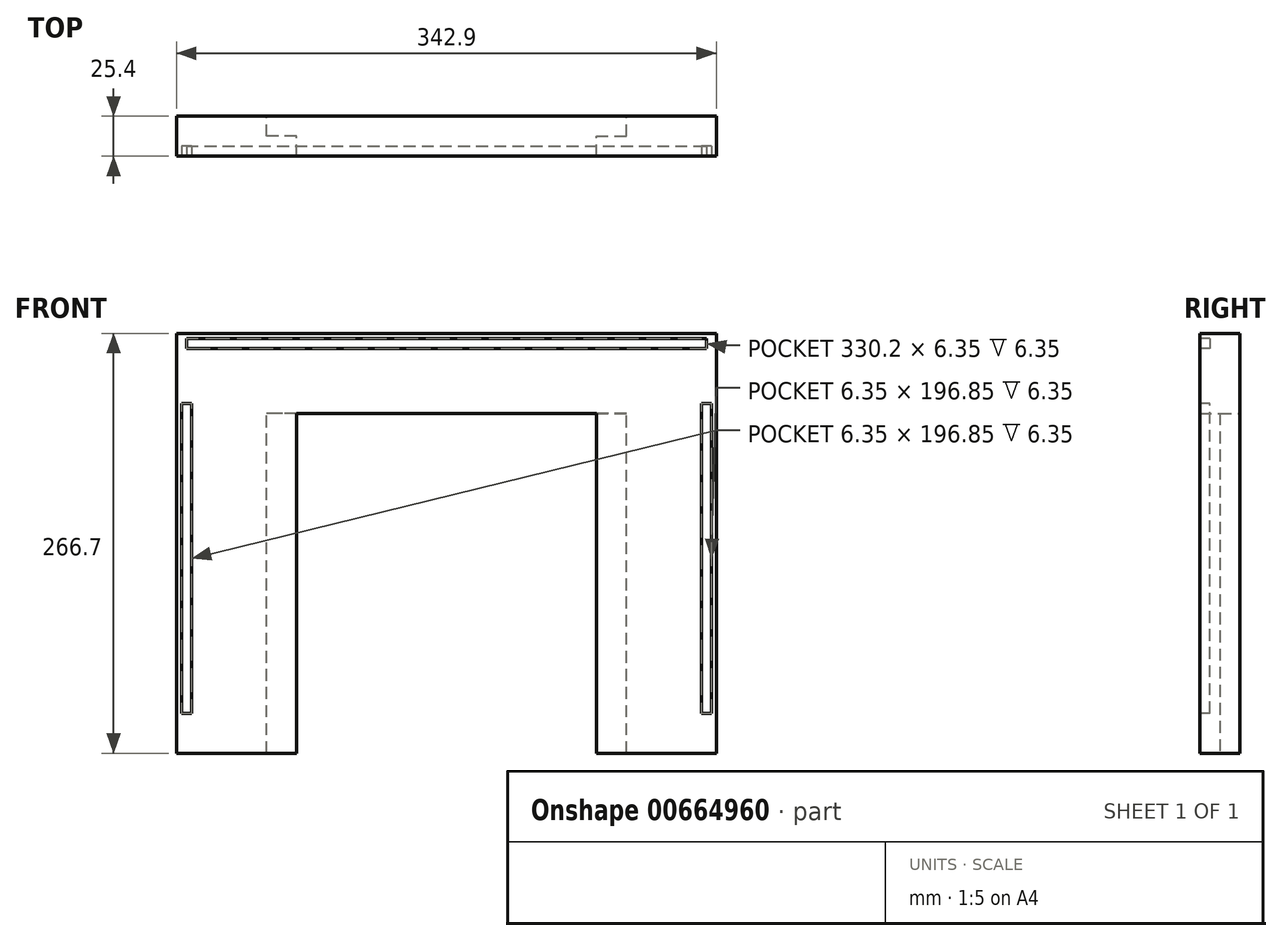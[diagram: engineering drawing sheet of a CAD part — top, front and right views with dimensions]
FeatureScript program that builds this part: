
annotation { "Feature Type Name" : "Feature", "Feature Type Description" : "" }
export const myFeature = defineFeature(function(context is Context, id is Id, definition is map)
    precondition{}
    {
        {
            var Q0;
            Q0=qCreatedBy(makeId("Front.planeOp"),FACE);
            var sketch = newSketch(context, id + "F0", { "sketchPlane" : qUnion([Q0])});
            skLineSegment(sketch, "E0.bottom", {"start": v(0, 0) * mm, "end": v(-342.9, 0) * mm});
            skLineSegment(sketch, "E0.top", {"start": v(0, 266.7) * mm, "end": v(-342.9, 266.7) * mm});
            skLineSegment(sketch, "E0.left", {"start": v(0, 0) * mm, "end": v(0, 266.7) * mm});
            skLineSegment(sketch, "E0.right", {"start": v(-342.9, 0) * mm, "end": v(-342.9, 266.7) * mm});
            skSolve(sketch);
        }
        {
            var Q0;
            Q0=makeQuery(id+"F0.imprint","IMPRINT",FACE,{"disambiguationData":[TD([[makeQuery(id+"F0.imprint","IMPRINT",EDGE,{"derivedFrom":sQuery(id+"F0.wireOp",EDGE,"E0.bottom")}),-1.0]])]});
            extrude(context, id + "F1", {"entities" : qUnion([Q0]), "depth" : 25.4 * mm, "offsetDistance" : 25.4 * mm});
        }
        {
            var Q0;
            Q0=makeQuery(id+"F1.opExtrude","CAP_FACE",FACE,{"disambiguationData":[OSD([sQuery(id+"F0.wireOp",EDGE,"E0.bottom"),sQuery(id+"F0.wireOp",EDGE,"E0.top"),sQuery(id+"F0.wireOp",EDGE,"E0.left"),sQuery(id+"F0.wireOp",EDGE,"E0.right")])],"isStart":true});
            var sketch = newSketch(context, id + "F2", { "sketchPlane" : qUnion([Q0])});
            skLineSegment(sketch, "E1.bottom", {"start": v(171.45, 0) * mm, "end": v(285.75, 0) * mm});
            skLineSegment(sketch, "E1.top", {"start": v(171.45, 215.9) * mm, "end": v(285.75, 215.9) * mm});
            skLineSegment(sketch, "E1.left", {"start": v(171.45, 0) * mm, "end": v(171.45, 215.9) * mm});
            skLineSegment(sketch, "E1.right", {"start": v(285.75, 0) * mm, "end": v(285.75, 215.9) * mm});
            skLineSegment(sketch, "E2.bottom", {"start": v(171.45, 0) * mm, "end": v(57.15, 0) * mm});
            skLineSegment(sketch, "E2.top", {"start": v(171.45, 215.9) * mm, "end": v(57.15, 215.9) * mm});
            skLineSegment(sketch, "E2.right", {"start": v(57.15, 0) * mm, "end": v(57.15, 215.9) * mm});
            skSolve(sketch);
        }
        {
            var Q0;
            Q0=makeQuery(id+"F2.imprint","IMPRINT",FACE,{"disambiguationData":[TD([[makeQuery(id+"F2.imprint","IMPRINT",EDGE,{"derivedFrom":sQuery(id+"F2.wireOp",EDGE,"E1.bottom")}),1.0]])]});
            var Q1;
            Q1=makeQuery(id+"F2.imprint","IMPRINT",FACE,{"disambiguationData":[TD([[makeQuery(id+"F2.imprint","IMPRINT",EDGE,{"derivedFrom":sQuery(id+"F2.wireOp",EDGE,"E2.bottom")}),1.0]])]});
            extrude(context, id + "F3", {"entities" : qUnion([Q0, Q1]), "operationType" : NewBodyOperationType.REMOVE, "oppositeDirection" : true, "depth" : 25.4 * mm, "offsetDistance" : 25.4 * mm});
        }
        {
            var Q0;
            Q0=makeQuery(id+"F3.boolean.opBoolean","COPY",FACE,{"derivedFrom":makeQuery(id+"F3.opExtrude","SWEPT_FACE",FACE,{"disambiguationData":[OSD([sQuery(id+"F2.wireOp",EDGE,"E1.right")])]})});
            var sketch = newSketch(context, id + "F4", { "sketchPlane" : qUnion([Q0])});
            skLineSegment(sketch, "E3.bottom", {"start": v(-25.4, 215.9) * mm, "end": v(-12.7, 215.9) * mm});
            skLineSegment(sketch, "E3.top", {"start": v(-25.4, 0) * mm, "end": v(-12.7, 0) * mm});
            skLineSegment(sketch, "E3.left", {"start": v(-25.4, 215.9) * mm, "end": v(-25.4, 0) * mm});
            skLineSegment(sketch, "E3.right", {"start": v(-12.7, 215.9) * mm, "end": v(-12.7, 0) * mm});
            skSolve(sketch);
        }
        {
            var Q0;
            Q0=makeQuery(id+"F4.imprint","IMPRINT",FACE,{"disambiguationData":[TD([[makeQuery(id+"F4.imprint","IMPRINT",EDGE,{"derivedFrom":sQuery(id+"F4.wireOp",EDGE,"E3.bottom")}),-1.0]])]});
            extrude(context, id + "F5", {"entities" : qUnion([Q0]), "operationType" : NewBodyOperationType.ADD, "depth" : 19.05 * mm, "offsetDistance" : 25.4 * mm});
        }
        {
            var Q0;
            Q0=makeQuery(id+"F3.boolean.opBoolean","COPY",FACE,{"derivedFrom":makeQuery(id+"F3.opExtrude","SWEPT_FACE",FACE,{"disambiguationData":[OSD([sQuery(id+"F2.wireOp",EDGE,"E2.right")])]})});
            var sketch = newSketch(context, id + "F6", { "sketchPlane" : qUnion([Q0])});
            skLineSegment(sketch, "E4.bottom", {"start": v(25.4, 215.9) * mm, "end": v(12.7, 215.9) * mm});
            skLineSegment(sketch, "E4.top", {"start": v(25.4, 0) * mm, "end": v(12.7, 0) * mm});
            skLineSegment(sketch, "E4.left", {"start": v(25.4, 215.9) * mm, "end": v(25.4, 0) * mm});
            skLineSegment(sketch, "E4.right", {"start": v(12.7, 215.9) * mm, "end": v(12.7, 0) * mm});
            skSolve(sketch);
        }
        {
            var Q0;
            Q0=makeQuery(id+"F6.imprint","IMPRINT",FACE,{"disambiguationData":[TD([[makeQuery(id+"F6.imprint","IMPRINT",EDGE,{"derivedFrom":sQuery(id+"F6.wireOp",EDGE,"E4.bottom")}),1.0]])]});
            extrude(context, id + "F7", {"entities" : qUnion([Q0]), "operationType" : NewBodyOperationType.ADD, "depth" : 19.05 * mm, "offsetDistance" : 25.4 * mm});
        }
        {
            var Q0;
            Q0=makeQuery(id+"F3.boolean.opBoolean","COPY",FACE,{"derivedFrom":makeQuery(id+"F3.opExtrude","SWEPT_FACE",FACE,{"disambiguationData":[OSD([sQuery(id+"F2.wireOp",EDGE,"E1.top"),sQuery(id+"F2.wireOp",EDGE,"E2.top")])]})});
            var sketch = newSketch(context, id + "F8", { "sketchPlane" : qUnion([Q0])});
            skLineSegment(sketch, "E5.bottom", {"start": v(-266.7, 25.4) * mm, "end": v(-76.2, 25.4) * mm});
            skLineSegment(sketch, "E5.top", {"start": v(-266.7, 12.7) * mm, "end": v(-76.2, 12.7) * mm});
            skLineSegment(sketch, "E5.left", {"start": v(-266.7, 25.4) * mm, "end": v(-266.7, 12.7) * mm});
            skLineSegment(sketch, "E5.right", {"start": v(-76.2, 25.4) * mm, "end": v(-76.2, 12.7) * mm});
            skSolve(sketch);
        }
        {
            var Q0;
            Q0=makeQuery(id+"Fjdorv49B3eqpX0_1.boolean.opBoolean","MERGE",FACE,{"derivedFrom":[makeQuery(id+"F7.boolean.opBoolean","MERGE",FACE,{"derivedFrom":[makeQuery(id+"F5.boolean.opBoolean","MERGE",FACE,{"derivedFrom":[makeQuery(id+"F1.opExtrude","CAP_FACE",FACE,{"disambiguationData":[OSD([sQuery(id+"F0.wireOp",EDGE,"E0.bottom"),sQuery(id+"F0.wireOp",EDGE,"E0.top"),sQuery(id+"F0.wireOp",EDGE,"E0.left"),sQuery(id+"F0.wireOp",EDGE,"E0.right")])],"isStart":false}),makeQuery(id+"F5.opExtrude","SWEPT_FACE",FACE,{"disambiguationData":[OSD([sQuery(id+"F4.wireOp",EDGE,"E3.left")])]})]}),makeQuery(id+"F7.opExtrude","SWEPT_FACE",FACE,{"disambiguationData":[OSD([sQuery(id+"F6.wireOp",EDGE,"E4.left")])]})]}),makeQuery(id+"Fjdorv49B3eqpX0_1.opExtrude","SWEPT_FACE",FACE,{"disambiguationData":[OSD([sQuery(id+"F8.wireOp",EDGE,"E5.bottom")])]})]});
            var sketch = newSketch(context, id + "F9", { "sketchPlane" : qUnion([Q0])});
            skLineSegment(sketch, "E6.bottom", {"start": v(-336.55, 263.53) * mm, "end": v(-6.35, 263.53) * mm});
            skLineSegment(sketch, "E6.top", {"start": v(-336.55, 257.18) * mm, "end": v(-6.35, 257.18) * mm});
            skLineSegment(sketch, "E6.left", {"start": v(-336.55, 263.53) * mm, "end": v(-336.55, 257.18) * mm});
            skLineSegment(sketch, "E6.right", {"start": v(-6.35, 263.53) * mm, "end": v(-6.35, 257.18) * mm});
            skSolve(sketch);
        }
        {
            var Q0;
            Q0=makeQuery(id+"F9.imprint","IMPRINT",FACE,{"disambiguationData":[TD([[makeQuery(id+"F9.imprint","IMPRINT",EDGE,{"derivedFrom":sQuery(id+"F9.wireOp",EDGE,"PN8EDpdX-UxKq-kTYa-kRhu-YVakBY7pK1H3")}),-1.0]])]});
            var Q1;
            Q1=makeQuery(id+"F9.imprint","IMPRINT",FACE,{"disambiguationData":[TD([[makeQuery(id+"F9.imprint","IMPRINT",EDGE,{"derivedFrom":sQuery(id+"F9.wireOp",EDGE,"E6.bottom")}),-1.0]])]});
            extrude(context, id + "F10", {"entities" : qUnion([Q0, Q1]), "operationType" : NewBodyOperationType.REMOVE, "oppositeDirection" : true, "depth" : 6.35 * mm, "offsetDistance" : 25.4 * mm});
        }
        {
            var Q0;
            {var subQ0=sQuery(id+"F9.wireOp",EDGE,"xqAtE8jZ-MSQi-wsMK-Cfxa-qjlJsnQtlB2g");var subQ1=sQuery(id+"F9.wireOp",EDGE,"wupwBbng-9ADD-dlqu-zdOx-LhtTEIHjZ5c6");var subQ2=sQuery(id+"F4.wireOp",EDGE,"E3.left");var subQ4=sQuery(id+"F0.wireOp",EDGE,"E0.left");var subQ6=sQuery(id+"F0.wireOp",EDGE,"E0.right");var subQ8=sQuery(id+"F0.wireOp",EDGE,"E0.bottom");var subQ9=sQuery(id+"F6.wireOp",EDGE,"E4.left");var subQ11=sQuery(id+"F8.wireOp",EDGE,"E5.bottom");var subQ12=sQuery(id+"F0.wireOp",EDGE,"E0.top");var subQ13=makeQuery(id+"Fjdorv49B3eqpX0_1.boolean.opBoolean","MERGE",FACE,{"derivedFrom":[makeQuery(id+"F7.boolean.opBoolean","MERGE",FACE,{"derivedFrom":[makeQuery(id+"F5.boolean.opBoolean","MERGE",FACE,{"derivedFrom":[makeQuery(id+"F1.opExtrude","CAP_FACE",FACE,{"disambiguationData":[OSD([subQ8,subQ12,subQ4,subQ6])],"isStart":false}),makeQuery(id+"F5.opExtrude","SWEPT_FACE",FACE,{"disambiguationData":[OSD([subQ2])]})]}),makeQuery(id+"F7.opExtrude","SWEPT_FACE",FACE,{"disambiguationData":[OSD([subQ9])]})]}),makeQuery(id+"Fjdorv49B3eqpX0_1.opExtrude","SWEPT_FACE",FACE,{"disambiguationData":[OSD([subQ11])]})]});Q0=makeQuery(id+"F0RdzGHNo0SqyFe_1.boolean.opBoolean","MERGE",FACE,{"derivedFrom":[makeQuery(id+"F10.boolean.opBoolean","SPLIT",FACE,{"disambiguationData":[TD([makeQuery(id+"F1.opExtrude","SWEPT_FACE",FACE,{"disambiguationData":[OSD([subQ12])]})])],"derivedFrom":subQ13}),makeQuery(id+"F10.boolean.opBoolean","SPLIT",FACE,{"disambiguationData":[TD([makeQuery(id+"F1.opExtrude","SWEPT_FACE",FACE,{"disambiguationData":[OSD([subQ8])]})])],"derivedFrom":subQ13}),makeQuery(id+"F0RdzGHNo0SqyFe_1.opExtrude","CAP_FACE",FACE,{"disambiguationData":[OSD([sQuery(id+"F9.wireOp",EDGE,"PN8EDpdX-UxKq-kTYa-kRhu-YVakBY7pK1H3"),subQ1,sQuery(id+"FOVAEcgDDyFFfZ8_1.wireOp",EDGE,"nz253aN8-FZ8S-CjIh-FSMk-9zDWw15Nw71U"),sQuery(id+"FOVAEcgDDyFFfZ8_1.wireOp",EDGE,"IQOgAqve-XtaT-q8pA-dEpv-JMt7KHQhdw9S")])],"isStart":false}),makeQuery(id+"F0RdzGHNo0SqyFe_1.opExtrude","CAP_FACE",FACE,{"disambiguationData":[OSD([sQuery(id+"F9.wireOp",EDGE,"x3UhV2a7-a52A-phkE-f1KC-NXz0k5Vd1l0W"),subQ0,sQuery(id+"FOVAEcgDDyFFfZ8_1.wireOp",EDGE,"QqpNMukD-AVh3-qdz0-PZfW-0oBNXRCXpbVx"),sQuery(id+"FOVAEcgDDyFFfZ8_1.wireOp",EDGE,"Gae9H1v8-NbSC-08h2-7QT0-SAaEcTMA60AD")])],"isStart":false})]});}
            var sketch = newSketch(context, id + "F11", { "sketchPlane" : qUnion([Q0])});
            skLineSegment(sketch, "E7", {"start": v(0, 266.7) * mm, "end": v(0, 222.25) * mm});
            skLineSegment(sketch, "E8", {"start": v(0, 222.25) * mm, "end": v(-3.17, 222.25) * mm});
            skLineSegment(sketch, "E9", {"start": v(-3.17, 222.25) * mm, "end": v(-9.52, 222.25) * mm});
            skLineSegment(sketch, "E10", {"start": v(-9.52, 222.25) * mm, "end": v(-9.52, 25.4) * mm});
            skLineSegment(sketch, "E11", {"start": v(-9.52, 25.4) * mm, "end": v(-3.17, 25.4) * mm});
            skLineSegment(sketch, "E12", {"start": v(-3.17, 25.4) * mm, "end": v(-3.17, 222.25) * mm});
            skLineSegment(sketch, "E13", {"start": v(-342.9, 266.7) * mm, "end": v(-342.9, 222.25) * mm});
            skLineSegment(sketch, "E14", {"start": v(-342.9, 222.25) * mm, "end": v(-339.73, 222.25) * mm});
            skLineSegment(sketch, "E15", {"start": v(-339.73, 222.25) * mm, "end": v(-339.73, 25.4) * mm});
            skLineSegment(sketch, "E16", {"start": v(-339.73, 25.4) * mm, "end": v(-333.38, 25.4) * mm});
            skLineSegment(sketch, "E17", {"start": v(-333.38, 25.4) * mm, "end": v(-333.38, 222.25) * mm});
            skLineSegment(sketch, "E18", {"start": v(-333.38, 222.25) * mm, "end": v(-339.73, 222.25) * mm});
            skSolve(sketch);
        }
        {
            var Q0;
            Q0=makeQuery(id+"F11.imprint","IMPRINT",FACE,{"disambiguationData":[TD([[makeQuery(id+"F11.imprint","IMPRINT",EDGE,{"derivedFrom":sQuery(id+"F11.wireOp",EDGE,"E15")}),1.0]])]});
            var Q1;
            Q1=makeQuery(id+"F11.imprint","IMPRINT",FACE,{"disambiguationData":[TD([[makeQuery(id+"F11.imprint","IMPRINT",EDGE,{"derivedFrom":sQuery(id+"F11.wireOp",EDGE,"E9")}),1.0]])]});
            extrude(context, id + "F12", {"entities" : qUnion([Q0, Q1]), "operationType" : NewBodyOperationType.REMOVE, "oppositeDirection" : true, "depth" : 6.35 * mm, "offsetDistance" : 25.4 * mm});
        }
    });
